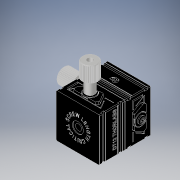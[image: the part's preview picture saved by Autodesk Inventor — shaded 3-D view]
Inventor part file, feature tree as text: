
AUTODESK INVENTOR PART (.ipt)
format: ipt  version: 2019 (Build 230136000, 136)  size: 4,397,056 bytes
history: native  units: in
note: dims shown in document units (in); Inventor stores cm internally (conversion verified against a paired STEP export)
features: other x31, plane x2
ambient origin geometry x8: Origin, YZ Plane, XZ Plane, XY Plane, X Axis, Y Axis, Z Axis, Center Point
bodies: Solid1 (feature_tree)
feature tree (33):
  other  "DT12XY-Step.iam"
  other  "134331 - fixed_world_imperial_134331.ipt:1"
  other  "134332 - moving_world_134332.ipt:1"
  other  "DB0381 - M4x4 Dog Point Set Screw_DB0381.ipt:1"
  other  "134335 - screw_holder_imperial_134335.ipt:1"
  other  "134333 - screw_134333.ipt:1"
  other  "134336 - guide_bush_134336.ipt:1"
  other  "134336 - guide_bush_134336.ipt:2"
  other  "134337 - flat spring_134337.ipt:1"
  other  "DF0118 - M3 DIN 433 Washer_DF0118.ipt:1"
  other  "DF0118 - M3 DIN 433 Washer_DF0118.ipt:2"
  other  "DF0115 - M3_nylon_washer_DF0115.ipt:1"
  other  "DF0115 - M3_nylon_washer_DF0115.ipt:2"
  other  "134338 - metal_knob_134338.ipt:1"
  other  "DB0193 - M2.5 x 3 Soc Set Screw_DB0193.ipt:1"
  other  "DB0219 M4x5 Skt Set_DB0219.ipt:1"
  other  "134331 - fixed_world_imperial_134331.ipt:2"
  other  "134332 - moving_world_134332.ipt:2"
  other  "DB0381 - M4x4 Dog Point Set Screw_DB0381.ipt:2"
  other  "134335 - screw_holder_imperial_134335.ipt:2"
  other  "134333 - screw_134333.ipt:2"
  other  "134336 - guide_bush_134336.ipt:3"
  other  "134336 - guide_bush_134336.ipt:4"
  other  "134337 - flat spring_134337.ipt:2"
  other  "DF0118 - M3 DIN 433 Washer_DF0118.ipt:3"
  other  "DF0118 - M3 DIN 433 Washer_DF0118.ipt:4"
  other  "DF0115 - M3_nylon_washer_DF0115.ipt:3"
  other  "DF0115 - M3_nylon_washer_DF0115.ipt:4"
  other  "134338 - metal_knob_134338.ipt:2"
  other  "DB0193 - M2.5 x 3 Soc Set Screw_DB0193.ipt:2"
  other  "DB0219 M4x5 Skt Set_DB0219.ipt:2"
  plane  "Work Plane1"
  plane  "Work Plane2"
